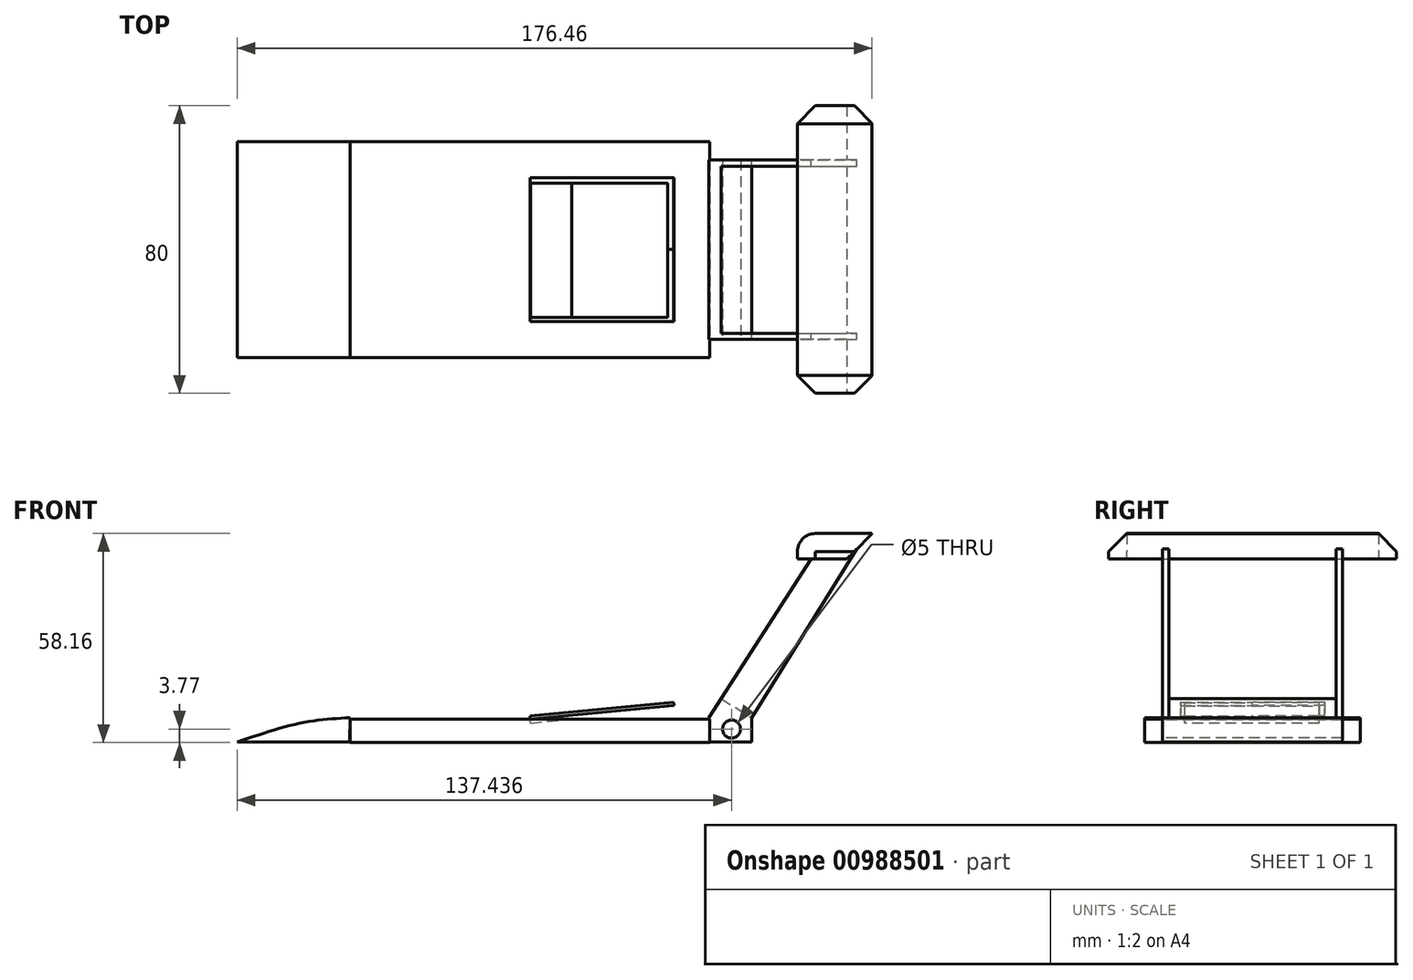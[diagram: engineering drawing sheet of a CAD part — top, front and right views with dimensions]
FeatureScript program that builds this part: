
annotation { "Feature Type Name" : "Feature", "Feature Type Description" : "" }
export const myFeature = defineFeature(function(context is Context, id is Id, definition is map)
    precondition{}
    {
        {
            var Q0;
            Q0=qCreatedBy(makeId("Front.planeOp"),FACE);
            var sketch = newSketch(context, id + "F0", { "sketchPlane" : qUnion([Q0])});
            skLineSegment(sketch, "E0.bottom", {"start": v(-16.67, 12.73) * mm, "end": v(83.33, 12.73) * mm});
            skLineSegment(sketch, "E0.top", {"start": v(-16.67, 6.23) * mm, "end": v(83.33, 6.23) * mm});
            skLineSegment(sketch, "E0.left", {"start": v(-16.67, 12.73) * mm, "end": v(-16.67, 6.23) * mm});
            skLineSegment(sketch, "E0.right", {"start": v(83.33, 12.73) * mm, "end": v(83.33, 6.23) * mm});
            skLineSegment(sketch, "E1", {"start": v(33.33, 12.73) * mm, "end": v(73.33, 16.55) * mm});
            skLineSegment(sketch, "E2", {"start": v(73.33, 16.55) * mm, "end": v(73.25, 17.45) * mm});
            skLineSegment(sketch, "E3", {"start": v(73.25, 17.45) * mm, "end": v(33.33, 13.63) * mm});
            skLineSegment(sketch, "E4", {"start": v(33.33, 13.63) * mm, "end": v(33.33, 12.73) * mm});
            skSolve(sketch);
        }
        {
            var Q0;
            Q0=makeQuery(id+"F0.imprint","IMPRINT",FACE,{"disambiguationData":[TD([[makeQuery(id+"F0.imprint","IMPRINT",EDGE,{"derivedFrom":sQuery(id+"F0.wireOp",EDGE,"E0.top")}),1.0]])]});
            extrude(context, id + "F1", {"entities" : qUnion([Q0]), "depth" : 30 * mm, "offsetDistance" : 25.4 * mm});
        }
        {
            var Q0;
            Q0=makeQuery(id+"F1.opExtrude","CAP_FACE",FACE,{"disambiguationData":[OSD([sQuery(id+"F0.wireOp",EDGE,"E0.bottom"),sQuery(id+"F0.wireOp",EDGE,"E0.top"),sQuery(id+"F0.wireOp",EDGE,"E0.left"),sQuery(id+"F0.wireOp",EDGE,"E0.right")])],"isStart":true});
            extrude(context, id + "F2", {"entities" : qUnion([Q0]), "operationType" : NewBodyOperationType.ADD, "depth" : 30 * mm, "offsetDistance" : 25 * mm});
        }
        {
            var Q0;
            Q0=makeQuery(id+"F0.imprint","IMPRINT",FACE,{"disambiguationData":[TD([[makeQuery(id+"F0.imprint","IMPRINT",EDGE,{"derivedFrom":sQuery(id+"F0.wireOp",EDGE,"E1")}),1.0]])]});
            extrude(context, id + "F3", {"entities" : qUnion([Q0]), "depth" : 20 * mm, "offsetDistance" : 25 * mm});
        }
        {
            var Q0;
            Q0=makeQuery(id+"F0.imprint","IMPRINT",FACE,{"disambiguationData":[TD([[makeQuery(id+"F0.imprint","IMPRINT",EDGE,{"derivedFrom":sQuery(id+"F0.wireOp",EDGE,"E1")}),1.0]])]});
            extrude(context, id + "F4", {"entities" : qUnion([Q0]), "oppositeDirection" : true, "depth" : 20 * mm, "offsetDistance" : 25 * mm});
        }
        {
            var Q0;
            Q0=makeQuery(id+"F4.opExtrude","SWEPT_FACE",FACE,{"disambiguationData":[OSD([sQuery(id+"F0.wireOp",EDGE,"E3")])]});
            var sketch = newSketch(context, id + "F5", { "sketchPlane" : qUnion([Q0])});
            skLineSegment(sketch, "E5.bottom", {"start": v(34.48, 18.47) * mm, "end": v(72.97, 18.47) * mm});
            skLineSegment(sketch, "E5.top", {"start": v(34.48, -18.13) * mm, "end": v(72.97, -18.13) * mm});
            skLineSegment(sketch, "E5.left", {"start": v(34.48, 18.47) * mm, "end": v(34.48, -18.13) * mm});
            skLineSegment(sketch, "E5.right", {"start": v(72.97, 18.47) * mm, "end": v(72.97, -18.13) * mm});
            skSolve(sketch);
        }
        {
            var Q0;
            {var subQ0=sQuery(id+"F5.wireOp",EDGE,"E5.bottom");Q0=makeQuery(id+"F5.imprint","IMPRINT",FACE,{"disambiguationData":[TD([[makeQuery(id+"F5.imprint","IMPRINT",EDGE,{"derivedFrom":subQ0}),-1.0]])]});}
            extrude(context, id + "F6", {"entities" : qUnion([Q0]), "operationType" : NewBodyOperationType.REMOVE, "oppositeDirection" : true, "depth" : 2 * mm, "offsetDistance" : 25 * mm});
        }
        {
            var Q0;
            Q0=makeQuery(id+"F3.opExtrude","SWEPT_FACE",FACE,{"disambiguationData":[OSD([sQuery(id+"F0.wireOp",EDGE,"E3")])]});
            var sketch = newSketch(context, id + "F7", { "sketchPlane" : qUnion([Q0])});
            skLineSegment(sketch, "E6.bottom", {"start": v(34.48, -18.85) * mm, "end": v(72.94, -18.85) * mm});
            skLineSegment(sketch, "E6.top", {"start": v(34.48, 1.07) * mm, "end": v(72.94, 1.07) * mm});
            skLineSegment(sketch, "E6.left", {"start": v(34.48, -18.85) * mm, "end": v(34.48, 1.07) * mm});
            skLineSegment(sketch, "E6.right", {"start": v(72.94, -18.85) * mm, "end": v(72.94, 1.07) * mm});
            skSolve(sketch);
        }
        {
            var Q0;
            {var subQ0=sQuery(id+"F7.wireOp",EDGE,"E6.bottom");Q0=makeQuery(id+"F7.imprint","IMPRINT",FACE,{"disambiguationData":[TD([[makeQuery(id+"F7.imprint","IMPRINT",EDGE,{"derivedFrom":subQ0}),1.0]])]});}
            extrude(context, id + "F8", {"entities" : qUnion([Q0]), "operationType" : NewBodyOperationType.REMOVE, "oppositeDirection" : true, "depth" : 2 * mm, "offsetDistance" : 25 * mm});
        }
        {
            var Q0;
            Q0=qCreatedBy(makeId("Front.planeOp"),FACE);
            var sketch = newSketch(context, id + "F9", { "sketchPlane" : qUnion([Q0])});
            skLineSegment(sketch, "E7.bottom", {"start": v(83.06, 13.17) * mm, "end": v(94.9, 13.17) * mm});
            skLineSegment(sketch, "E7.top", {"start": v(83.06, 6.37) * mm, "end": v(94.9, 6.37) * mm});
            skLineSegment(sketch, "E7.left", {"start": v(83.06, 13.17) * mm, "end": v(83.06, 6.37) * mm});
            skLineSegment(sketch, "E7.right", {"start": v(94.9, 13.17) * mm, "end": v(94.9, 6.37) * mm});
            skLineSegment(sketch, "E8", {"start": v(94.9, 13.17) * mm, "end": v(122.44, 57.29) * mm});
            skLineSegment(sketch, "E9", {"start": v(122.44, 57.29) * mm, "end": v(111.48, 57.29) * mm});
            skLineSegment(sketch, "E10", {"start": v(111.48, 57.29) * mm, "end": v(83.06, 13.17) * mm});
            skLineSegment(sketch, "E11", {"start": v(-17.6, 6.37) * mm, "end": v(-48.09, 6.37) * mm});
            skFitSpline(sketch, "E12", {"points": [v(-48.09, 6.37) * mm, v(-30.32, 11.7) * mm, v(-16.7, 13.17) * mm], "startDerivative": vector(33.99, 11.71) * mm, "endDerivative": vector(28.64, 1.65) * mm});
            skLineSegment(sketch, "E13", {"start": v(-17.6, 6.37) * mm, "end": v(-16.74, 6.37) * mm});
            skLineSegment(sketch, "E14", {"start": v(-16.74, 6.37) * mm, "end": v(-16.7, 13.17) * mm});
            skSolve(sketch);
        }
        {
            var Q0;
            Q0=makeQuery(id+"F9.imprint","IMPRINT",FACE,{"disambiguationData":[TD([[makeQuery(id+"F9.imprint","IMPRINT",EDGE,{"derivedFrom":sQuery(id+"F9.wireOp",EDGE,"E7.bottom")}),-1.0]])]});
            var Q1;
            Q1=makeQuery(id+"F9.imprint","IMPRINT",FACE,{"disambiguationData":[TD([[makeQuery(id+"F9.imprint","IMPRINT",EDGE,{"derivedFrom":sQuery(id+"F9.wireOp",EDGE,"E7.bottom")}),1.0]])]});
            extrude(context, id + "F10", {"entities" : qUnion([Q0, Q1]), "operationType" : NewBodyOperationType.ADD, "depth" : 25 * mm, "offsetDistance" : 25 * mm});
        }
        {
            var Q0;
            Q0=makeQuery(id+"F10.opExtrude","CAP_FACE",FACE,{"disambiguationData":[OSD([sQuery(id+"F9.wireOp",EDGE,"E7.top"),sQuery(id+"F9.wireOp",EDGE,"E7.left"),sQuery(id+"F9.wireOp",EDGE,"E7.right"),sQuery(id+"F9.wireOp",EDGE,"E8"),sQuery(id+"F9.wireOp",EDGE,"E9"),sQuery(id+"F9.wireOp",EDGE,"E10")])],"isStart":true});
            extrude(context, id + "F11", {"entities" : qUnion([Q0]), "operationType" : NewBodyOperationType.ADD, "depth" : 25 * mm, "offsetDistance" : 25 * mm});
        }
        {
            var Q0;
            Q0=makeQuery(id+"F9.imprint","IMPRINT",FACE,{"disambiguationData":[TD([[makeQuery(id+"F9.imprint","IMPRINT",EDGE,{"derivedFrom":sQuery(id+"F9.wireOp",EDGE,"E11")}),-1.0]])]});
            extrude(context, id + "F12", {"entities" : qUnion([Q0]), "depth" : 30 * mm, "offsetDistance" : 25 * mm});
        }
        {
            var Q0;
            Q0=makeQuery(id+"F9.imprint","IMPRINT",FACE,{"disambiguationData":[TD([[makeQuery(id+"F9.imprint","IMPRINT",EDGE,{"derivedFrom":sQuery(id+"F9.wireOp",EDGE,"E11")}),-1.0]])]});
            extrude(context, id + "F13", {"entities" : qUnion([Q0]), "operationType" : NewBodyOperationType.ADD, "oppositeDirection" : true, "depth" : 30 * mm, "offsetDistance" : 25 * mm});
        }
        {
            var Q0;
            {var subQ0=sQuery(id+"F9.wireOp",EDGE,"E8");Q0=makeQuery(id+"F11.boolean.opBoolean","MERGE",FACE,{"derivedFrom":[makeQuery(id+"F10.opExtrude","SWEPT_FACE",FACE,{"disambiguationData":[OSD([subQ0])]}),makeQuery(id+"F11.opExtrude","SWEPT_FACE",FACE,{"disambiguationData":[OSD([subQ0])]})]});}
            var sketch = newSketch(context, id + "F14", { "sketchPlane" : qUnion([Q0])});
            skLineSegment(sketch, "E15.bottom", {"start": v(-23.26, 61.43) * mm, "end": v(23.21, 61.43) * mm});
            skLineSegment(sketch, "E15.top", {"start": v(-23.26, 113.43) * mm, "end": v(23.21, 113.43) * mm});
            skLineSegment(sketch, "E15.left", {"start": v(-23.26, 61.43) * mm, "end": v(-23.26, 113.43) * mm});
            skLineSegment(sketch, "E15.right", {"start": v(23.21, 61.43) * mm, "end": v(23.21, 113.43) * mm});
            skSolve(sketch);
        }
        {
            var Q0;
            Q0=makeQuery(id+"F14.imprint","IMPRINT",FACE,{"disambiguationData":[TD([[makeQuery(id+"F14.imprint","IMPRINT",EDGE,{"derivedFrom":sQuery(id+"F14.wireOp",EDGE,"E15.bottom")}),1.0]])]});
            extrude(context, id + "F15", {"entities" : qUnion([Q0]), "operationType" : NewBodyOperationType.REMOVE, "oppositeDirection" : true, "depth" : 25 * mm, "offsetDistance" : 25 * mm});
        }
        {
            var Q0;
            Q0=qCreatedBy(makeId("Front.planeOp"),FACE);
            var sketch = newSketch(context, id + "F16", { "sketchPlane" : qUnion([Q0])});
            skLineSegment(sketch, "E16.bottom", {"start": v(107.65, 57.29) * mm, "end": v(128.37, 57.29) * mm});
            skLineSegment(sketch, "E16.top", {"start": v(107.65, 64.4) * mm, "end": v(128.37, 64.4) * mm});
            skLineSegment(sketch, "E16.left", {"start": v(107.65, 57.29) * mm, "end": v(107.65, 64.4) * mm});
            skLineSegment(sketch, "E16.right", {"start": v(128.37, 57.29) * mm, "end": v(128.37, 64.4) * mm});
            skSolve(sketch);
        }
        {
            var Q0;
            Q0=makeQuery(id+"F16.imprint","IMPRINT",FACE,{"disambiguationData":[TD([[makeQuery(id+"F16.imprint","IMPRINT",EDGE,{"derivedFrom":sQuery(id+"F16.wireOp",EDGE,"E16.bottom")}),1.0]])]});
            extrude(context, id + "F17", {"entities" : qUnion([Q0]), "operationType" : NewBodyOperationType.ADD, "depth" : 40 * mm, "offsetDistance" : 25 * mm});
        }
        {
            var Q0;
            Q0=makeQuery(id+"F17.opExtrude","CAP_FACE",FACE,{"disambiguationData":[OSD([sQuery(id+"F16.wireOp",EDGE,"E16.bottom"),sQuery(id+"F16.wireOp",EDGE,"E16.top"),sQuery(id+"F16.wireOp",EDGE,"E16.left"),sQuery(id+"F16.wireOp",EDGE,"E16.right")])],"isStart":true});
            extrude(context, id + "F18", {"entities" : qUnion([Q0]), "operationType" : NewBodyOperationType.ADD, "depth" : 40 * mm, "offsetDistance" : 25 * mm});
        }
        {
            var Q0;
            {var subQ0=sQuery(id+"F16.wireOp",EDGE,"E16.left");var subQ1=sQuery(id+"F16.wireOp",EDGE,"E16.top");Q0=makeQuery(id+"F18.boolean.opBoolean","MERGE",EDGE,{"derivedFrom":[makeQuery(id+"F17.opExtrude","SWEPT_EDGE",EDGE,{"disambiguationData":[OSD([subQ1,subQ0])]}),makeQuery(id+"F18.opExtrude","SWEPT_EDGE",EDGE,{"disambiguationData":[OSD([subQ1,subQ0])]})]});}
            fillet(context, id + "F19", {"entities" : qUnion([Q0]), "radius" : 5 * mm, "tangentPropagation" : true, "allowEdgeOverflow" : false});
        }
        {
            var Q0;
            {var subQ0=sQuery(id+"F16.wireOp",EDGE,"E16.right");var subQ1=sQuery(id+"F16.wireOp",EDGE,"E16.bottom");Q0=makeQuery(id+"F18.boolean.opBoolean","MERGE",EDGE,{"derivedFrom":[makeQuery(id+"F17.opExtrude","SWEPT_EDGE",EDGE,{"disambiguationData":[OSD([subQ1,subQ0])]}),makeQuery(id+"F18.opExtrude","SWEPT_EDGE",EDGE,{"disambiguationData":[OSD([subQ1,subQ0])]})]});}
            chamfer(context, id + "F20", {"entities" : qUnion([Q0]), "width" : 7 * mm, "tangentPropagation" : true});
        }
        {
            var Q0;
            {var subQ0=sQuery(id+"F16.wireOp",EDGE,"E16.left");var subQ1=sQuery(id+"F16.wireOp",EDGE,"E16.top");Q0=makeQuery(id+"F19.opFillet","BLEND_EDGE",EDGE,{"blendedFrom":[makeQuery(id+"F18.boolean.opBoolean","MERGE",EDGE,{"derivedFrom":[makeQuery(id+"F17.opExtrude","SWEPT_EDGE",EDGE,{"disambiguationData":[OSD([subQ1,subQ0])]}),makeQuery(id+"F18.opExtrude","SWEPT_EDGE",EDGE,{"disambiguationData":[OSD([subQ1,subQ0])]})]}),makeQuery(id+"F18.opExtrude","CAP_FACE",FACE,{"disambiguationData":[OSD([sQuery(id+"F16.wireOp",EDGE,"E16.bottom"),subQ1,subQ0,sQuery(id+"F16.wireOp",EDGE,"E16.right")])],"isStart":false})],"blendedInto":[makeQuery(id+"F18.opExtrude","CAP_FACE",FACE,{"disambiguationData":[OSD([sQuery(id+"F16.wireOp",EDGE,"E16.bottom"),subQ1,subQ0,sQuery(id+"F16.wireOp",EDGE,"E16.right")])],"isStart":false})]});}
            var Q1;
            {var subQ0=sQuery(id+"F16.wireOp",EDGE,"E16.left");var subQ1=sQuery(id+"F16.wireOp",EDGE,"E16.top");Q1=makeQuery(id+"F19.opFillet","BLEND_EDGE",EDGE,{"blendedFrom":[makeQuery(id+"F18.boolean.opBoolean","MERGE",EDGE,{"derivedFrom":[makeQuery(id+"F17.opExtrude","SWEPT_EDGE",EDGE,{"disambiguationData":[OSD([subQ1,subQ0])]}),makeQuery(id+"F18.opExtrude","SWEPT_EDGE",EDGE,{"disambiguationData":[OSD([subQ1,subQ0])]})]}),makeQuery(id+"F17.opExtrude","CAP_FACE",FACE,{"disambiguationData":[OSD([sQuery(id+"F16.wireOp",EDGE,"E16.bottom"),subQ1,subQ0,sQuery(id+"F16.wireOp",EDGE,"E16.right")])],"isStart":false})],"blendedInto":[makeQuery(id+"F17.opExtrude","CAP_FACE",FACE,{"disambiguationData":[OSD([sQuery(id+"F16.wireOp",EDGE,"E16.bottom"),subQ1,subQ0,sQuery(id+"F16.wireOp",EDGE,"E16.right")])],"isStart":false})]});}
            chamfer(context, id + "F21", {"entities" : qUnion([Q0, Q1]), "width" : 5 * mm, "tangentPropagation" : true});
        }
        {
            var Q0;
            Q0=makeQuery(id+"F10.opExtrude","CAP_FACE",FACE,{"disambiguationData":[OSD([sQuery(id+"F9.wireOp",EDGE,"E7.top"),sQuery(id+"F9.wireOp",EDGE,"E7.left"),sQuery(id+"F9.wireOp",EDGE,"E7.right"),sQuery(id+"F9.wireOp",EDGE,"E8"),sQuery(id+"F9.wireOp",EDGE,"E9"),sQuery(id+"F9.wireOp",EDGE,"E10")])],"isStart":false});
            var sketch = newSketch(context, id + "F22", { "sketchPlane" : qUnion([Q0])});
            skCircle(sketch, "E17", {"center": v(89.35, 10) * mm, "radius": 2.5 * mm});
            skSolve(sketch);
        }
        {
            var Q0;
            Q0=makeQuery(id+"F22.imprint","IMPRINT",FACE,{"disambiguationData":[TD([[makeQuery(id+"F22.imprint","IMPRINT",EDGE,{"derivedFrom":sQuery(id+"F22.wireOp",EDGE,"E17")}),1.0]])]});
            extrude(context, id + "F23", {"entities" : qUnion([Q0]), "operationType" : NewBodyOperationType.REMOVE, "surfaceOperationType" : NewSurfaceOperationType.ADD, "oppositeDirection" : true, "depth" : 60 * mm, "offsetDistance" : 25 * mm});
        }
    });
